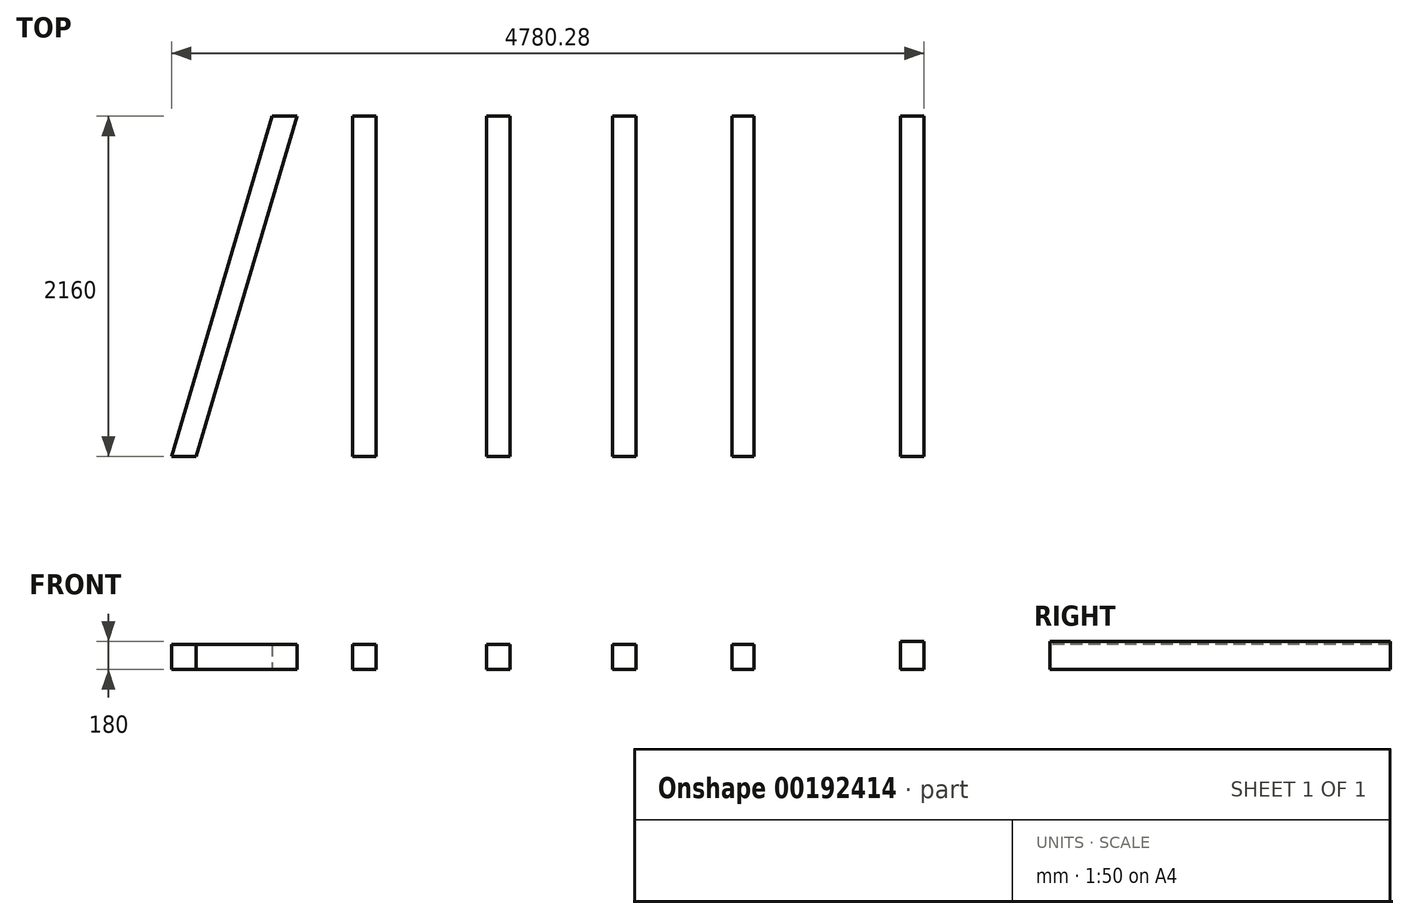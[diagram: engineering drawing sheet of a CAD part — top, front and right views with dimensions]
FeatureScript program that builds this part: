
annotation { "Feature Type Name" : "Feature", "Feature Type Description" : "" }
export const myFeature = defineFeature(function(context is Context, id is Id, definition is map)
    precondition{}
    {
        {
            var Q0;
            Q0=qCreatedBy(makeId("Top.planeOp"),FACE);
            var sketch = newSketch(context, id + "F0", { "sketchPlane" : qUnion([Q0])});
            skLineSegment(sketch, "E0.bottom", {"start": v(-75, 1080) * mm, "end": v(75, 1080) * mm});
            skLineSegment(sketch, "E0.top", {"start": v(-75, -1080) * mm, "end": v(75, -1080) * mm});
            skLineSegment(sketch, "E0.left", {"start": v(-75, 1080) * mm, "end": v(-75, -1080) * mm});
            skLineSegment(sketch, "E0.right", {"start": v(75, 1080) * mm, "end": v(75, -1080) * mm});
            skPoint(sketch, "E0.middle", {"position": v(0, 0) * mm});
            skLineSegment(sketch, "E1.bottom", {"start": v(725, 1080) * mm, "end": v(875, 1080) * mm});
            skLineSegment(sketch, "E1.top", {"start": v(725, -1080) * mm, "end": v(875, -1080) * mm});
            skLineSegment(sketch, "E1.left", {"start": v(725, 1080) * mm, "end": v(725, -1080) * mm});
            skLineSegment(sketch, "E1.right", {"start": v(875, 1080) * mm, "end": v(875, -1080) * mm});
            skLineSegment(sketch, "E2.bottom", {"start": v(1485, 1080) * mm, "end": v(1625, 1080) * mm});
            skLineSegment(sketch, "E2.top", {"start": v(1485, -1080) * mm, "end": v(1625, -1080) * mm});
            skLineSegment(sketch, "E2.left", {"start": v(1485, 1080) * mm, "end": v(1485, -1080) * mm});
            skLineSegment(sketch, "E2.right", {"start": v(1625, 1080) * mm, "end": v(1625, -1080) * mm});
            skLineSegment(sketch, "E3.bottom", {"start": v(2555, 1080) * mm, "end": v(2705, 1080) * mm});
            skLineSegment(sketch, "E3.top", {"start": v(2555, -1080) * mm, "end": v(2705, -1080) * mm});
            skLineSegment(sketch, "E3.left", {"start": v(2555, 1080) * mm, "end": v(2555, -1080) * mm});
            skLineSegment(sketch, "E3.right", {"start": v(2705, 1080) * mm, "end": v(2705, -1080) * mm});
            skLineSegment(sketch, "E4.bottom", {"start": v(-775, 1080) * mm, "end": v(-925, 1080) * mm});
            skLineSegment(sketch, "E4.top", {"start": v(-775, -1080) * mm, "end": v(-925, -1080) * mm});
            skLineSegment(sketch, "E4.left", {"start": v(-775, 1080) * mm, "end": v(-775, -1080) * mm});
            skLineSegment(sketch, "E4.right", {"start": v(-925, 1080) * mm, "end": v(-925, -1080) * mm});
            skLineSegment(sketch, "E5", {"start": v(-1278.83, 1080) * mm, "end": v(-1918.83, -1080) * mm});
            skLineSegment(sketch, "E6", {"start": v(-1918.83, -1080) * mm, "end": v(-2075.28, -1080) * mm});
            skLineSegment(sketch, "E7", {"start": v(-2075.28, -1080) * mm, "end": v(-1435.28, 1080) * mm});
            skLineSegment(sketch, "E8", {"start": v(-1435.28, 1080) * mm, "end": v(-1278.83, 1080) * mm});
            skSolve(sketch);
        }
        {
            var Q0;
            Q0=makeQuery(id+"F0.imprint","IMPRINT",FACE,{"disambiguationData":[TD([[makeQuery(id+"F0.imprint","IMPRINT",EDGE,{"derivedFrom":sQuery(id+"F0.wireOp",EDGE,"E5")}),-1.0]])]});
            var Q1;
            Q1=makeQuery(id+"F0.imprint","IMPRINT",FACE,{"disambiguationData":[TD([[makeQuery(id+"F0.imprint","IMPRINT",EDGE,{"derivedFrom":sQuery(id+"F0.wireOp",EDGE,"E4.bottom")}),1.0]])]});
            var Q2;
            Q2=makeQuery(id+"F0.imprint","IMPRINT",FACE,{"disambiguationData":[TD([[makeQuery(id+"F0.imprint","IMPRINT",EDGE,{"derivedFrom":sQuery(id+"F0.wireOp",EDGE,"E0.bottom")}),-1.0]])]});
            var Q3;
            Q3=makeQuery(id+"F0.imprint","IMPRINT",FACE,{"disambiguationData":[TD([[makeQuery(id+"F0.imprint","IMPRINT",EDGE,{"derivedFrom":sQuery(id+"F0.wireOp",EDGE,"E1.bottom")}),-1.0]])]});
            var Q4;
            Q4=makeQuery(id+"F0.imprint","IMPRINT",FACE,{"disambiguationData":[TD([[makeQuery(id+"F0.imprint","IMPRINT",EDGE,{"derivedFrom":sQuery(id+"F0.wireOp",EDGE,"E2.bottom")}),-1.0]])]});
            extrude(context, id + "F1", {"entities" : qUnion([Q0, Q1, Q2, Q3, Q4]), "depth" : 160 * mm});
        }
        {
            var Q0;
            Q0=makeQuery(id+"F0.imprint","IMPRINT",FACE,{"disambiguationData":[TD([[makeQuery(id+"F0.imprint","IMPRINT",EDGE,{"derivedFrom":sQuery(id+"F0.wireOp",EDGE,"E3.bottom")}),-1.0]])]});
            extrude(context, id + "F2", {"entities" : qUnion([Q0]), "depth" : 180 * mm});
        }
    });
